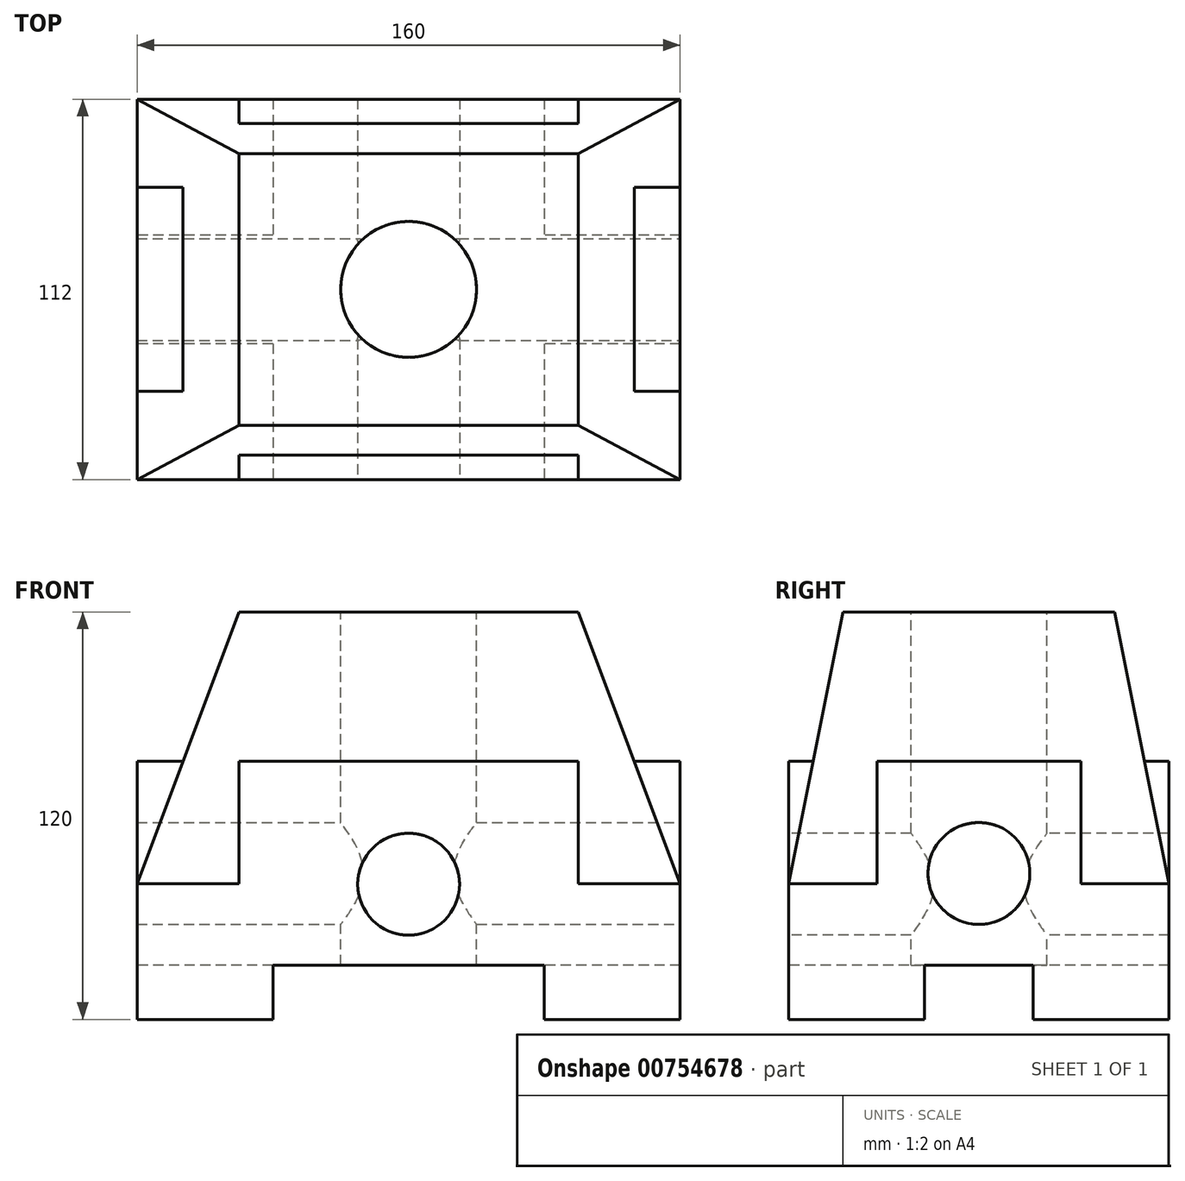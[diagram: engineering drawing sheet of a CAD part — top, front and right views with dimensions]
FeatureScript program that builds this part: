
annotation { "Feature Type Name" : "Feature", "Feature Type Description" : "" }
export const myFeature = defineFeature(function(context is Context, id is Id, definition is map)
    precondition{}
    {
        {
            var Q0;
            Q0=qCreatedBy(makeId("Top.planeOp"),FACE);
            var sketch = newSketch(context, id + "F0", { "sketchPlane" : qUnion([Q0])});
            skLineSegment(sketch, "E0.bottom", {"start": v(80, 56) * mm, "end": v(-80, 56) * mm});
            skLineSegment(sketch, "E0.top", {"start": v(80, -56) * mm, "end": v(-80, -56) * mm});
            skLineSegment(sketch, "E0.left", {"start": v(80, 56) * mm, "end": v(80, -56) * mm});
            skLineSegment(sketch, "E0.right", {"start": v(-80, 56) * mm, "end": v(-80, -56) * mm});
            skPoint(sketch, "E0.middle", {"position": v(0, 0) * mm});
            skSolve(sketch);
        }
        {
            var Q0;
            Q0=makeQuery(id+"F0.imprint","IMPRINT",FACE,{"disambiguationData":[TD([[makeQuery(id+"F0.imprint","IMPRINT",EDGE,{"derivedFrom":sQuery(id+"F0.wireOp",EDGE,"E0.bottom")}),1.0]])]});
            extrude(context, id + "F1", {"entities" : qUnion([Q0]), "depth" : 40 * mm, "offsetDistance" : 25 * mm});
        }
        {
            var Q0;
            Q0=makeQuery(id+"F1.opExtrude","SWEPT_FACE",FACE,{"disambiguationData":[OSD([sQuery(id+"F0.wireOp",EDGE,"E0.top")])]});
            var sketch = newSketch(context, id + "F2", { "sketchPlane" : qUnion([Q0])});
            skLineSegment(sketch, "E1.bottom", {"start": v(-40, 0) * mm, "end": v(40, 0) * mm});
            skLineSegment(sketch, "E1.top", {"start": v(-40, 16) * mm, "end": v(40, 16) * mm});
            skLineSegment(sketch, "E1.left", {"start": v(-40, 0) * mm, "end": v(-40, 16) * mm});
            skLineSegment(sketch, "E1.right", {"start": v(40, 0) * mm, "end": v(40, 16) * mm});
            skSolve(sketch);
        }
        {
            var Q0;
            Q0=makeQuery(id+"F2.imprint","IMPRINT",FACE,{"disambiguationData":[TD([[makeQuery(id+"F2.imprint","IMPRINT",EDGE,{"derivedFrom":sQuery(id+"F2.wireOp",EDGE,"E1.bottom")}),-1.0]])]});
            extrude(context, id + "F3", {"entities" : qUnion([Q0]), "operationType" : NewBodyOperationType.REMOVE, "oppositeDirection" : true, "depth" : 112 * mm, "offsetDistance" : 25 * mm});
        }
        {
            var Q0;
            Q0=makeQuery(id+"F1.opExtrude","SWEPT_FACE",FACE,{"disambiguationData":[OSD([sQuery(id+"F0.wireOp",EDGE,"E0.right")])]});
            var sketch = newSketch(context, id + "F4", { "sketchPlane" : qUnion([Q0])});
            skLineSegment(sketch, "E2.bottom", {"start": v(-16, 0) * mm, "end": v(16, 0) * mm});
            skLineSegment(sketch, "E2.top", {"start": v(-16, 16) * mm, "end": v(16, 16) * mm});
            skLineSegment(sketch, "E2.left", {"start": v(-16, 0) * mm, "end": v(-16, 16) * mm});
            skLineSegment(sketch, "E2.right", {"start": v(16, 0) * mm, "end": v(16, 16) * mm});
            skSolve(sketch);
        }
        {
            var Q0;
            Q0=makeQuery(id+"F4.imprint","IMPRINT",FACE,{"disambiguationData":[TD([[makeQuery(id+"F4.imprint","IMPRINT",EDGE,{"derivedFrom":sQuery(id+"F4.wireOp",EDGE,"E2.bottom")}),1.0]])]});
            extrude(context, id + "F5", {"entities" : qUnion([Q0]), "operationType" : NewBodyOperationType.REMOVE, "oppositeDirection" : true, "depth" : 160 * mm, "offsetDistance" : 25 * mm});
        }
        {
            var Q0;
            Q0=makeQuery(id+"F1.opExtrude","CAP_FACE",FACE,{"disambiguationData":[OSD([sQuery(id+"F0.wireOp",EDGE,"E0.bottom"),sQuery(id+"F0.wireOp",EDGE,"E0.top"),sQuery(id+"F0.wireOp",EDGE,"E0.left"),sQuery(id+"F0.wireOp",EDGE,"E0.right")])],"isStart":false});
            var sketch = newSketch(context, id + "F6", { "sketchPlane" : qUnion([Q0])});
            skLineSegment(sketch, "E3.bottom", {"start": v(-50, 56) * mm, "end": v(50, 56) * mm});
            skLineSegment(sketch, "E3.top", {"start": v(-50, -56) * mm, "end": v(50, -56) * mm});
            skLineSegment(sketch, "E3.left", {"start": v(-50, 56) * mm, "end": v(-50, -56) * mm});
            skLineSegment(sketch, "E3.right", {"start": v(50, 56) * mm, "end": v(50, -56) * mm});
            skSolve(sketch);
        }
        {
            var Q0;
            Q0=makeQuery(id+"F6.imprint","IMPRINT",FACE,{"disambiguationData":[TD([[makeQuery(id+"F6.imprint","IMPRINT",EDGE,{"derivedFrom":sQuery(id+"F6.wireOp",EDGE,"E3.bottom")}),1.0]])]});
            extrude(context, id + "F7", {"entities" : qUnion([Q0]), "operationType" : NewBodyOperationType.ADD, "depth" : 36 * mm, "offsetDistance" : 25 * mm});
        }
        {
            var Q0;
            {var subQ0=sQuery(id+"F0.wireOp",EDGE,"E0.bottom");var subQ1=sQuery(id+"F0.wireOp",EDGE,"E0.left");var subQ2=sQuery(id+"F0.wireOp",EDGE,"E0.top");Q0=makeQuery(id+"F7.boolean.opBoolean","SPLIT",FACE,{"disambiguationData":[TD([makeQuery(id+"F1.opExtrude","SWEPT_FACE",FACE,{"disambiguationData":[OSD([subQ1])]})])],"derivedFrom":makeQuery(id+"F1.opExtrude","CAP_FACE",FACE,{"disambiguationData":[OSD([subQ0,subQ2,subQ1,sQuery(id+"F0.wireOp",EDGE,"E0.right")])],"isStart":false})});}
            var sketch = newSketch(context, id + "F8", { "sketchPlane" : qUnion([Q0])});
            skLineSegment(sketch, "E4.bottom", {"start": v(50, 30) * mm, "end": v(80, 30) * mm});
            skLineSegment(sketch, "E4.top", {"start": v(50, -30) * mm, "end": v(80, -30) * mm});
            skLineSegment(sketch, "E4.left", {"start": v(50, 30) * mm, "end": v(50, -30) * mm});
            skLineSegment(sketch, "E4.right", {"start": v(80, 30) * mm, "end": v(80, -30) * mm});
            skSolve(sketch);
        }
        {
            var Q0;
            Q0=makeQuery(id+"F8.imprint","IMPRINT",FACE,{"disambiguationData":[TD([[makeQuery(id+"F8.imprint","IMPRINT",EDGE,{"derivedFrom":sQuery(id+"F8.wireOp",EDGE,"E4.bottom")}),-1.0]])]});
            extrude(context, id + "F9", {"entities" : qUnion([Q0]), "operationType" : NewBodyOperationType.ADD, "depth" : 36 * mm, "offsetDistance" : 25 * mm});
        }
        {
            var Q0;
            {var subQ0=sQuery(id+"F0.wireOp",EDGE,"E0.bottom");var subQ1=sQuery(id+"F0.wireOp",EDGE,"E0.top");var subQ2=sQuery(id+"F0.wireOp",EDGE,"E0.right");Q0=makeQuery(id+"F7.boolean.opBoolean","SPLIT",FACE,{"disambiguationData":[TD([makeQuery(id+"F1.opExtrude","SWEPT_FACE",FACE,{"disambiguationData":[OSD([subQ2])]})])],"derivedFrom":makeQuery(id+"F1.opExtrude","CAP_FACE",FACE,{"disambiguationData":[OSD([subQ0,subQ1,sQuery(id+"F0.wireOp",EDGE,"E0.left"),subQ2])],"isStart":false})});}
            var sketch = newSketch(context, id + "F10", { "sketchPlane" : qUnion([Q0])});
            skLineSegment(sketch, "E5.bottom", {"start": v(-80, 30) * mm, "end": v(-50, 30) * mm});
            skLineSegment(sketch, "E5.top", {"start": v(-80, -30) * mm, "end": v(-50, -30) * mm});
            skLineSegment(sketch, "E5.left", {"start": v(-80, 30) * mm, "end": v(-80, -30) * mm});
            skLineSegment(sketch, "E5.right", {"start": v(-50, 30) * mm, "end": v(-50, -30) * mm});
            skSolve(sketch);
        }
        {
            var Q0;
            Q0=makeQuery(id+"F10.imprint","IMPRINT",FACE,{"disambiguationData":[TD([[makeQuery(id+"F10.imprint","IMPRINT",EDGE,{"derivedFrom":sQuery(id+"F10.wireOp",EDGE,"E5.bottom")}),-1.0]])]});
            extrude(context, id + "F11", {"entities" : qUnion([Q0]), "operationType" : NewBodyOperationType.ADD, "depth" : 36 * mm, "offsetDistance" : 25 * mm});
        }
        {
            var Q0;
            Q0=qCreatedBy(makeId("Top.planeOp"),FACE);
            cPlane(context, id + "F12", {"entities" : qUnion([Q0]), "cplaneType" : CPlaneType.OFFSET, "offset" : 40 * mm, "width" : 150 * mm, "height" : 150 * mm});
        }
        {
            var Q0;
            Q0=qCreatedBy(id+"F12.planeOp",FACE);
            var sketch = newSketch(context, id + "F13", { "sketchPlane" : qUnion([Q0])});
            skLineSegment(sketch, "E6.bottom", {"start": v(80, 56) * mm, "end": v(-80, 56) * mm});
            skLineSegment(sketch, "E6.top", {"start": v(80, -56) * mm, "end": v(-80, -56) * mm});
            skLineSegment(sketch, "E6.left", {"start": v(80, 56) * mm, "end": v(80, -56) * mm});
            skLineSegment(sketch, "E6.right", {"start": v(-80, 56) * mm, "end": v(-80, -56) * mm});
            skPoint(sketch, "E6.middle", {"position": v(0, 0) * mm});
            skSolve(sketch);
        }
        {
            var Q0;
            Q0=qCreatedBy(makeId("Top.planeOp"),FACE);
            cPlane(context, id + "F14", {"entities" : qUnion([Q0]), "cplaneType" : CPlaneType.OFFSET, "offset" : 120 * mm, "width" : 150 * mm, "height" : 150 * mm});
        }
        {
            var Q0;
            Q0=qCreatedBy(id+"F14.planeOp",FACE);
            var sketch = newSketch(context, id + "F15", { "sketchPlane" : qUnion([Q0])});
            skLineSegment(sketch, "E7.bottom", {"start": v(50, 40) * mm, "end": v(-50, 40) * mm});
            skLineSegment(sketch, "E7.top", {"start": v(50, -40) * mm, "end": v(-50, -40) * mm});
            skLineSegment(sketch, "E7.left", {"start": v(50, 40) * mm, "end": v(50, -40) * mm});
            skLineSegment(sketch, "E7.right", {"start": v(-50, 40) * mm, "end": v(-50, -40) * mm});
            skPoint(sketch, "E7.middle", {"position": v(0, 0) * mm});
            skSolve(sketch);
        }
        {
            var Q1;
            Q1=makeQuery(id+"F15.imprint","IMPRINT",FACE,{"disambiguationData":[TD([[makeQuery(id+"F15.imprint","IMPRINT",EDGE,{"derivedFrom":sQuery(id+"F15.wireOp",EDGE,"E7.bottom")}),1.0]])]});
            var Q2;
            Q2=makeQuery(id+"F13.imprint","IMPRINT",FACE,{"disambiguationData":[TD([[makeQuery(id+"F13.imprint","IMPRINT",EDGE,{"derivedFrom":sQuery(id+"F13.wireOp",EDGE,"E6.bottom")}),1.0]])]});
            loft(context, id + "F16", {"operationType" : NewBodyOperationType.ADD, "sheetProfilesArray" : [{ "sheetProfileEntities" : qUnion([Q1]) }, { "sheetProfileEntities" : qUnion([Q2]) }]});
        }
        {
            var Q0;
            Q0=qCreatedBy(id+"F14.planeOp",FACE);
            var sketch = newSketch(context, id + "F17", { "sketchPlane" : qUnion([Q0])});
            skCircle(sketch, "E8", {"center": v(0, 0) * mm, "radius": 20 * mm});
            skSolve(sketch);
        }
        {
            var Q0;
            Q0=makeQuery(id+"F17.imprint","IMPRINT",FACE,{"disambiguationData":[TD([[makeQuery(id+"F17.imprint","IMPRINT",EDGE,{"derivedFrom":sQuery(id+"F17.wireOp",EDGE,"E8")}),1.0]])]});
            extrude(context, id + "F18", {"entities" : qUnion([Q0]), "operationType" : NewBodyOperationType.REMOVE, "oppositeDirection" : true, "depth" : 120 * mm, "offsetDistance" : 25 * mm});
        }
        {
            var Q0;
            Q0=makeQuery(id+"F9.boolean.opBoolean","MERGE",FACE,{"derivedFrom":[makeQuery(id+"F1.opExtrude","SWEPT_FACE",FACE,{"disambiguationData":[OSD([sQuery(id+"F0.wireOp",EDGE,"E0.left")])]}),makeQuery(id+"F9.opExtrude","SWEPT_FACE",FACE,{"disambiguationData":[OSD([sQuery(id+"F8.wireOp",EDGE,"E4.right")])]})]});
            var sketch = newSketch(context, id + "F19", { "sketchPlane" : qUnion([Q0])});
            skCircle(sketch, "E9", {"center": v(0, 42.97) * mm, "radius": 15 * mm});
            skSolve(sketch);
        }
        {
            var Q0;
            Q0=makeQuery(id+"F19.imprint","IMPRINT",FACE,{"disambiguationData":[TD([[makeQuery(id+"F19.imprint","IMPRINT",EDGE,{"derivedFrom":sQuery(id+"F19.wireOp",EDGE,"E9")}),1.0]])]});
            extrude(context, id + "F20", {"entities" : qUnion([Q0]), "operationType" : NewBodyOperationType.REMOVE, "oppositeDirection" : true, "depth" : 160 * mm, "offsetDistance" : 25 * mm});
        }
        {
            var Q0;
            Q0=makeQuery(id+"F7.boolean.opBoolean","MERGE",FACE,{"derivedFrom":[makeQuery(id+"F1.opExtrude","SWEPT_FACE",FACE,{"disambiguationData":[OSD([sQuery(id+"F0.wireOp",EDGE,"E0.top")])]}),makeQuery(id+"F7.opExtrude","SWEPT_FACE",FACE,{"disambiguationData":[OSD([sQuery(id+"F6.wireOp",EDGE,"E3.top")])]})]});
            var sketch = newSketch(context, id + "F21", { "sketchPlane" : qUnion([Q0])});
            skCircle(sketch, "E10", {"center": v(0, 39.8) * mm, "radius": 15 * mm});
            skSolve(sketch);
        }
        {
            var Q0;
            Q0=makeQuery(id+"F21.imprint","IMPRINT",FACE,{"disambiguationData":[TD([[makeQuery(id+"F21.imprint","IMPRINT",EDGE,{"derivedFrom":sQuery(id+"F21.wireOp",EDGE,"E10")}),1.0]])]});
            extrude(context, id + "F22", {"entities" : qUnion([Q0]), "operationType" : NewBodyOperationType.REMOVE, "oppositeDirection" : true, "depth" : 112 * mm, "offsetDistance" : 25 * mm});
        }
    });
